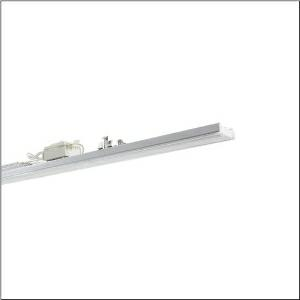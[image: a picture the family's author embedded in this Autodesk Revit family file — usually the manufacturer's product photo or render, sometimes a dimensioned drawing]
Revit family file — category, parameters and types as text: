
# Revit family: licross_r__21_recessed_mo_52tl18mn4a5g_8984
name_source: partatom
category: Lighting Fixtures
units: mm (PartAtom-declared; Revit-internal decimal feet)

## family parameters
Cut with Voids When Loaded = No
Host = Face
Light Source = No
Part Type = Normal
Room Calculation Point = No
Round Connector Dimension = Use Diameter
Shared = No

## types (1)
- --- (1 x LED, 10680 lm, 60.5 W, 4000K)
    Apparent Load = 61 VA
    CIE Flux Codes = 79 95 99 100 100
    Color Rendering = 80
    Color Temperature = 4000K
    Default Elevation = 1800 mm
    Description = Licross® 21 Recessed MO, luminaire insert, of sheet steel, galvanised, coil coated, white, length: 1.500mm, width: 66mm, height: 67mm, LED rated luminous flux: 10.680lm, light colour: 840, control gear: ON/OFF Multilumen, with plug, 3-pole, with phase selection, mains connection: 220..240V, AC, 50/60Hz, rated input power: 61W, halogen-free wiring, primary light control with lens, of plastic, primary optical cover: cover, of PMMA, light emission: direct distribution, primary light characteristic: symmetric, protection rating (complete): IP40, insulation class (complete): insulation class I (protective earthing), certification: CE, ENEC, VDE, UKCA, protection symbol: D if used in an environment without relevant dust loads with corresponding accessories, impact resistance: IK06, permissible ambient temperature for indoor applications: -35..+40°C, corresponds to IFS (International Featured Standards) requirements for safety and quality in the food industry, reducing of maximum allowable ambient temperature of 5°C with ceiling mounting, LABS conformity tested according to VDMA 24364:2018-05, packaging unit: 1 piece
    Height = 58 mm
    Lamp = 1 x LED
    Lamp Light Flux = 10680 lm
    Lamp Power = 60.5 W
    Lamp count = 1
    Length = 1500 mm
    Luminous efficacy = 177 lm/W
    Manufacturer = Siteco
    ModVariant = No
    Model = 52TL18MN4A5G
    Mounting Place = Ceiling
    Mounting Type = Pendant
    Number of Poles = 1
    OnlyDefault = Yes
    Power Factor = 1
    Product Name = Licross® 21 Recessed MO
    Product group = luminaire insert
    ProductGroupID = 902
    Protection Class = Protection class I
    Protection Degree = IP 40
    RLX_Detail_Level = 1
    RLX_Emergency_Light_Flux = 0 lm
    RLX_Emergency_Type = 0
    RLX_Emergency_Type_DB = No
    RlxData = <blob elided: 22217 chars, md5=694b5b6b>
    Socket = socket
    Standby Power = 0 W
    System Light Flux = 10680 lm
    System Power = 61 W
    Type Comments = factory setting: luminous flux: 100 % | (A | C | E) | 140 mA
    Type Image = l_1296930.jpg
    URL = http://relux.com
    VarID = @adj_108002
    Voltage = 0 V
    Weight = 0.00 kg
    Width = 66 mm

## geometry (parser evidence)
native form markers: Blend x4, Sweep x13
no freeform markers — native parametric forms only
